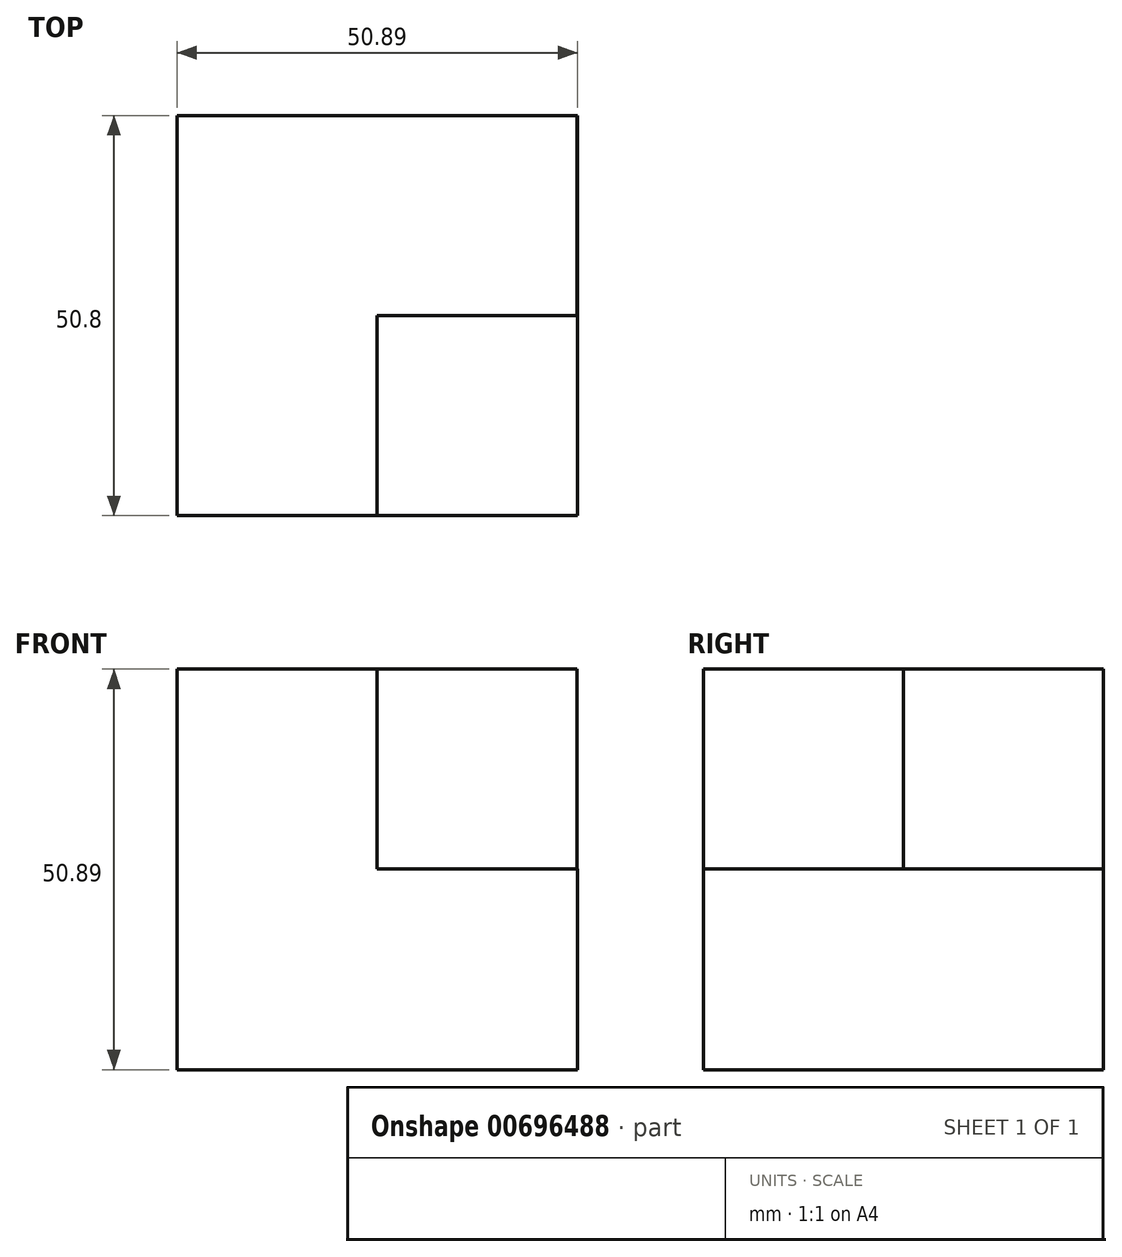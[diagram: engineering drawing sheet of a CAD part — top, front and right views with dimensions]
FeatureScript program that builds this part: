
annotation { "Feature Type Name" : "Feature", "Feature Type Description" : "" }
export const myFeature = defineFeature(function(context is Context, id is Id, definition is map)
    precondition{}
    {
        {
            var Q0;
            Q0=qCreatedBy(makeId("Front.planeOp"),FACE);
            var sketch = newSketch(context, id + "F0", { "sketchPlane" : qUnion([Q0])});
            skLineSegment(sketch, "E0.bottom", {"start": v(0, 0) * mm, "end": v(50.89, 0) * mm});
            skLineSegment(sketch, "E0.top", {"start": v(0, 50.89) * mm, "end": v(50.89, 50.89) * mm});
            skLineSegment(sketch, "E0.left", {"start": v(0, 0) * mm, "end": v(0, 50.89) * mm});
            skLineSegment(sketch, "E0.right", {"start": v(50.89, 0) * mm, "end": v(50.89, 50.89) * mm});
            skSolve(sketch);
        }
        {
            var Q0;
            Q0 = qSketchRegion(id + "F0", true);
            extrude(context, id + "F1", {"entities" : qUnion([Q0]), "depth" : 50.8 * mm, "offsetDistance" : 25.4 * mm});
        }
        {
            var Q0;
            Q0=makeQuery(id+"F1.opExtrude","CAP_FACE",FACE,{"disambiguationData":[OSD([sQuery(id+"F0.wireOp",EDGE,"E0.bottom"),sQuery(id+"F0.wireOp",EDGE,"E0.top"),sQuery(id+"F0.wireOp",EDGE,"E0.left"),sQuery(id+"F0.wireOp",EDGE,"E0.right")])],"isStart":false});
            var sketch = newSketch(context, id + "F2", { "sketchPlane" : qUnion([Q0])});
            skLineSegment(sketch, "E1", {"start": v(25.44, 50.89) * mm, "end": v(25.44, 25.5) * mm});
            skLineSegment(sketch, "E2", {"start": v(25.44, 25.5) * mm, "end": v(50.89, 25.5) * mm});
            skLineSegment(sketch, "E3", {"start": v(25.44, 50.89) * mm, "end": v(50.89, 50.89) * mm});
            skLineSegment(sketch, "E4", {"start": v(50.89, 25.5) * mm, "end": v(50.89, 50.89) * mm});
            skSolve(sketch);
        }
        {
            var Q0;
            Q0=makeQuery(id+"F2.imprint","IMPRINT",FACE,{"disambiguationData":[TD([[makeQuery(id+"F2.imprint","IMPRINT",EDGE,{"derivedFrom":sQuery(id+"F2.wireOp",EDGE,"E1")}),1.0]])]});
            extrude(context, id + "F3", {"entities" : qUnion([Q0]), "operationType" : NewBodyOperationType.REMOVE, "oppositeDirection" : true, "depth" : 50.8 * mm, "offsetDistance" : 25.4 * mm});
        }
        {
            var Q0;
            Q0=makeQuery(id+"F3.boolean.opBoolean","COPY",FACE,{"derivedFrom":makeQuery(id+"F3.opExtrude","SWEPT_FACE",FACE,{"disambiguationData":[OSD([sQuery(id+"F2.wireOp",EDGE,"E1")])]})});
            var sketch = newSketch(context, id + "F4", { "sketchPlane" : qUnion([Q0])});
            skLineSegment(sketch, "E5", {"start": v(-25.4, 50.89) * mm, "end": v(-25.4, 25.5) * mm});
            skLineSegment(sketch, "E6", {"start": v(-25.4, 25.5) * mm, "end": v(0, 25.5) * mm});
            skLineSegment(sketch, "E7", {"start": v(0, 50.89) * mm, "end": v(0, 43.37) * mm});
            skLineSegment(sketch, "E8", {"start": v(0, 50.89) * mm, "end": v(-25.4, 50.89) * mm});
            skLineSegment(sketch, "E9", {"start": v(0, 43.37) * mm, "end": v(0, 29.24) * mm});
            skSolve(sketch);
        }
        {
            var Q0;
            Q0=makeQuery(id+"F4.imprint","IMPRINT",FACE,{"disambiguationData":[TD([[makeQuery(id+"F4.imprint","IMPRINT",EDGE,{"derivedFrom":sQuery(id+"F4.wireOp",EDGE,"E5")}),1.0]])]});
            extrude(context, id + "F5", {"entities" : qUnion([Q0]), "operationType" : NewBodyOperationType.ADD, "depth" : 25.4 * mm, "offsetDistance" : 25.4 * mm});
        }
    });
